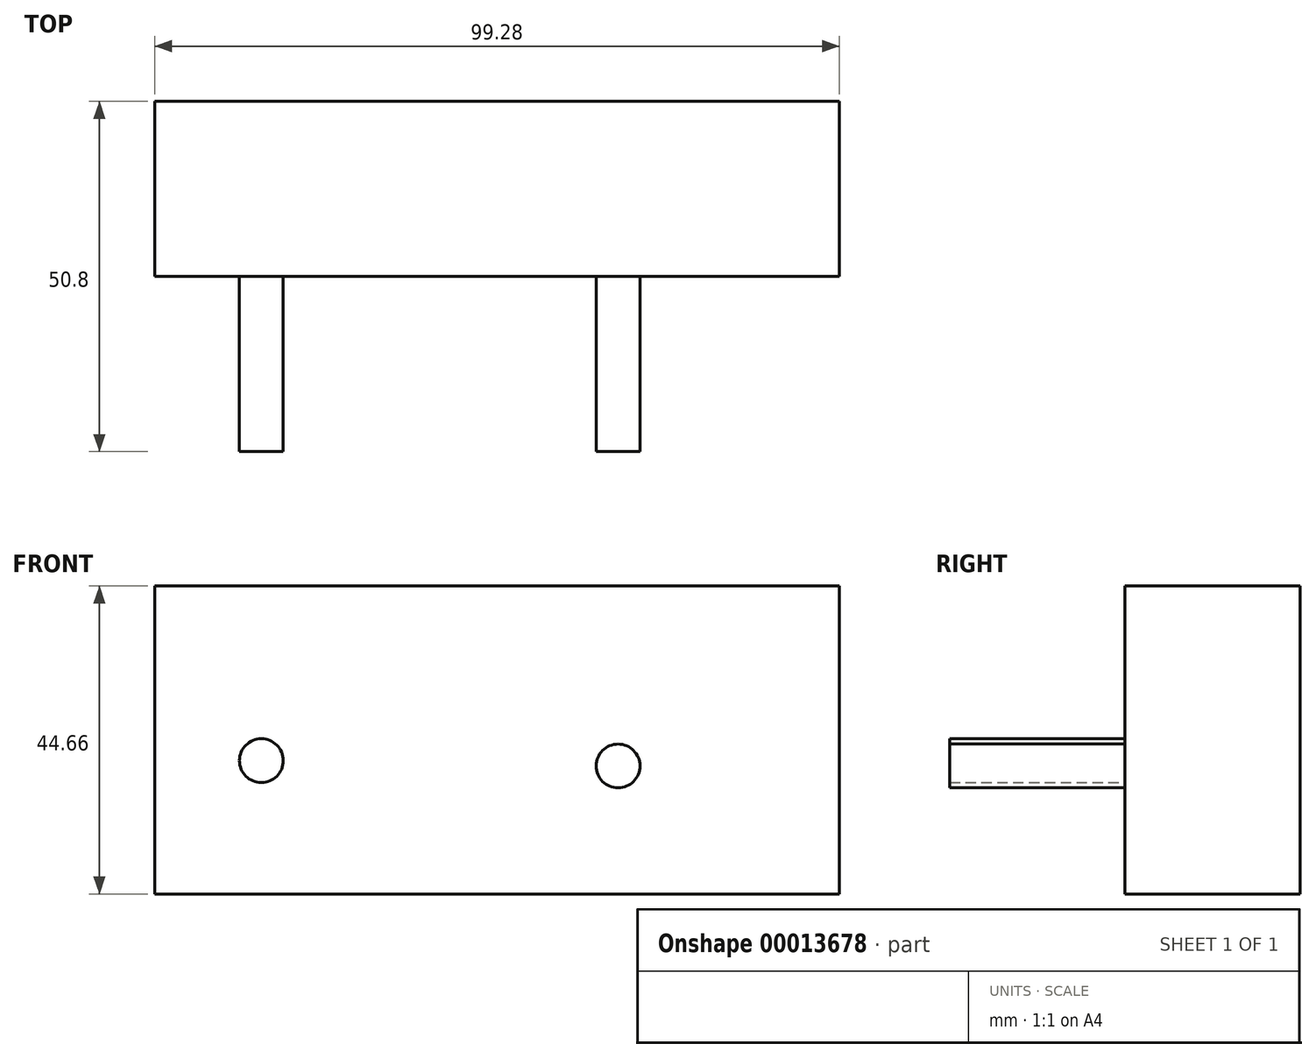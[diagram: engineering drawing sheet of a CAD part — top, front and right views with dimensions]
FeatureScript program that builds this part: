
annotation { "Feature Type Name" : "Feature", "Feature Type Description" : "" }
export const myFeature = defineFeature(function(context is Context, id is Id, definition is map)
    precondition{}
    {
        {
            var Q0;
            Q0=qCreatedBy(makeId("Front.planeOp"),FACE);
            var sketch = newSketch(context, id + "F0", { "sketchPlane" : qUnion([Q0])});
            skLineSegment(sketch, "E0.bottom", {"start": v(-45.3, 21.8) * mm, "end": v(53.98, 21.8) * mm});
            skLineSegment(sketch, "E0.top", {"start": v(-45.3, -22.86) * mm, "end": v(53.98, -22.86) * mm});
            skLineSegment(sketch, "E0.left", {"start": v(-45.3, 21.8) * mm, "end": v(-45.3, -22.86) * mm});
            skLineSegment(sketch, "E0.right", {"start": v(53.98, 21.8) * mm, "end": v(53.98, -22.86) * mm});
            skSolve(sketch);
        }
        {
            var Q0;
            Q0=makeQuery(id+"F0.imprint","IMPRINT",FACE,{"disambiguationData":[TD([[makeQuery(id+"F0.imprint","IMPRINT",EDGE,{"derivedFrom":sQuery(id+"F0.wireOp",EDGE,"E0.bottom")}),-1.0]])]});
            extrude(context, id + "F1", {"entities" : qUnion([Q0]), "depth" : 25.4 * mm});
        }
        {
            var Q0;
            Q0=makeQuery(id+"F1.opExtrude","CAP_FACE",FACE,{"disambiguationData":[OSD([sQuery(id+"F0.wireOp",EDGE,"E0.bottom"),sQuery(id+"F0.wireOp",EDGE,"E0.top"),sQuery(id+"F0.wireOp",EDGE,"E0.left"),sQuery(id+"F0.wireOp",EDGE,"E0.right")])],"isStart":false});
            var sketch = newSketch(context, id + "F2", { "sketchPlane" : qUnion([Q0])});
            skCircle(sketch, "E1", {"center": v(-29.81, -3.53) * mm, "radius": 3.18 * mm});
            skCircle(sketch, "E2", {"center": v(21.9, -4.3) * mm, "radius": 3.18 * mm});
            skSolve(sketch);
        }
        {
            var Q0;
            Q0 = qSketchRegion(id + "F2", true);
            extrude(context, id + "F3", {"entities" : qUnion([Q0]), "operationType" : NewBodyOperationType.ADD, "depth" : 25.4 * mm});
        }
    });
